# Revit family: JC KONTAKTER JCK265 Armbågskontakt
name_source: partatom
category: Specialty Equipment
units: mm (PartAtom-declared; Revit-internal decimal feet)

## family parameters
Always vertical = Yes
Cut with Voids When Loaded = No
Enable Cutting in Views = Yes
Host = Wall
Maintain Annotation Orientation = No
Part Type = Normal
Room Calculation Point = No
Round Connector Dimension = Use Diameter
Shared = No

## types (1)
- Armbågskontakt JCK265
    Antal mikrobrytare = 1
    Antal mikrobrytare 2 = 1
    CE Dokument = https://jckontakter.se
    Core Finish = Aluminum ENAW 6060
    Default Elevation = 0 mm  [stored 0 ft]
    Description = JCK265 är endast 50mm bred och utvecklad för montering på glaspartier byggda med 50mm profilsystem, samt i andra utrymmen där det är begränsat med plats. Modellen har dubbla tryckytor och är tillverkad i svarteloxerad aluminium med vita endcaps. Båda tryckytorna är utformade med taktila rillor och fungerar som extra vägledning för personer med synnedsättning. Man kan enkelt känna sig till vart man ska trycka för att aktivera dörröppning.

Våra armbågskontakter med dubbla tryckytor är utvecklade för miljöer med dubbla slagdörrar och gör det möjligt att styra varje dörr separat med en egen tryckknapp. Funktionen bidrar till att minska kallras och drag, samt spar energi jämfört med att båda dörrar åker upp vid varje öppning. Dessa armbågskontakter kan även vara lämpliga i en passage där det finns två ingångar till lokalen.
    End Cap Finish = POM Tenac C 4520 (Vit)
    Lid Finish = Aluminum ENAW 6060 (Svart)
    Lägsta märkström = 1mA/4 V DC
    Manufacturer = JC Kontakter
    Mikrobrytare 1 = Standard NC IP67 (Tre ledare)
    Mikrobrytare 2 = Standard NO IP67
    Model = JCK265
    Nominell märkström = 12 V - Resistive 6A Inductive L/R 5ms 6A, 24 V - Resistive 6A Inductive L/R 5ms 5A
    Placering av armbågskontakt = https://jckontakter.se
    Produktvikt = 0.318 kg
    Tekniskt produktblad = chrome-extension://efaidnbmnnnibpcajpcglclefindmkaj/https://jckontakter.se
    Tillvalsförteckning = https://jckontakter.se
    Tillverkningsland = Sverige
    URL = https://jckontakter.se

note: [stored X ft] marks values corroborated as IEEE doubles in the binary element streams (Revit-internal decimal feet)

## geometry (parser evidence)
native form markers: Sweep x8
no freeform markers — native parametric forms only
